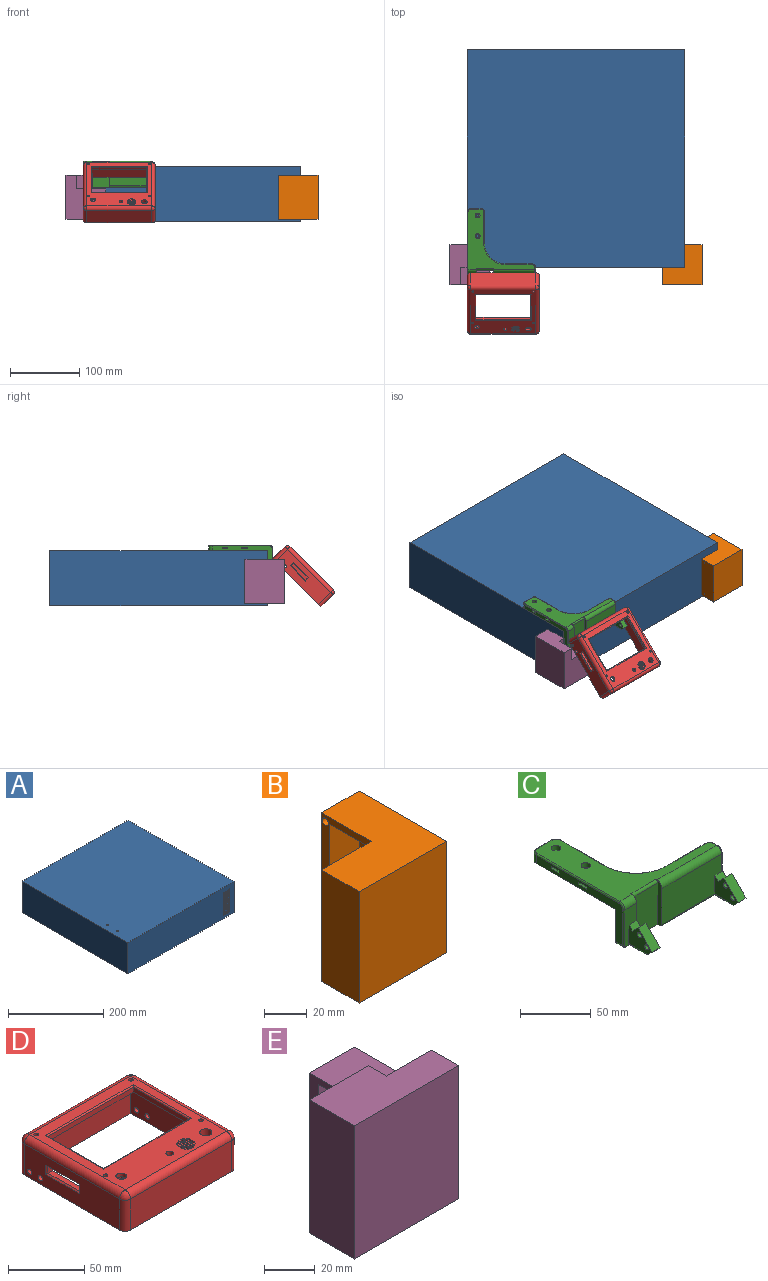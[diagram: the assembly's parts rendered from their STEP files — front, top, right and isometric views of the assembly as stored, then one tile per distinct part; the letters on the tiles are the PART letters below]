
ASSEMBLY  parts=5 mates=11
PART A: 40 faces, bbox 315x315x80 mm
  f0: plane 315x80mm, normal (1,0,0), area 24527.4mm2, adj f1,f3,f4,f5,f21,f22,f23,f24
  f1: plane 315x80mm, normal (0,-1,0), area 24527.4mm2, adj f0,f2,f4,f5,f6,f7,f8,f9
  f2: plane 315x80mm, normal (-1,0,0), area 25200mm2, adj f1,f3,f4,f5
  f3: plane 315x80mm, normal (0,1,0), area 25200mm2, adj f0,f2,f4,f5
  f4: plane 315x315mm, normal (0,0,1), area 99199.9mm2, adj f0,f1,f2,f3,f36,f38
  f5: plane 315x315mm, normal (0,0,-1), area 99225mm2, adj f0,f1,f2,f3
  f6: plane 59x1.5mm, normal (1,0,0), area 88.5mm2, adj f1,f7,f9,f10
  f7: plane 3.8x1.5mm, normal (0,0,1), area 5.7mm2, adj f1,f6,f8,f10
  f8: plane 59x1.5mm, normal (-1,0,0), area 88.5mm2, adj f1,f7,f9,f10
  f9: plane 3.8x1.5mm, normal (0,0,-1), area 5.7mm2, adj f1,f6,f8,f10
  f10: plane 59x3.8mm, normal (0,-1,0), area 224.2mm2, adj f6,f7,f8,f9
  f11: plane 59x1.5mm, normal (1,0,0), area 88.5mm2, adj f1,f12,f14,f15
  f12: plane 3.8x1.5mm, normal (0,0,1), area 5.7mm2, adj f1,f11,f13,f15
  f13: plane 59x1.5mm, normal (-1,0,0), area 88.5mm2, adj f1,f12,f14,f15
  f14: plane 3.8x1.5mm, normal (0,0,-1), area 5.7mm2, adj f1,f11,f13,f15
  f15: plane 59x3.8mm, normal (0,-1,0), area 224.2mm2, adj f11,f12,f13,f14
  f16: plane 3.8x1.5mm, normal (0,0,-1), area 5.7mm2, adj f1,f17,f19,f20
  f17: plane 59x1.5mm, normal (1,0,0), area 88.5mm2, adj f1,f16,f18,f20
  f18: plane 3.8x1.5mm, normal (0,0,1), area 5.7mm2, adj f1,f17,f19,f20
  f19: plane 59x1.5mm, normal (-1,0,0), area 88.5mm2, adj f1,f16,f18,f20
  f20: plane 59x3.8mm, normal (0,-1,0), area 224.2mm2, adj f16,f17,f18,f19
  f21: plane 59x1.5mm, normal (0,1,0), area 88.5mm2, adj f0,f22,f24,f25
  f22: plane 3.8x1.5mm, normal (0,0,1), area 5.7mm2, adj f0,f21,f23,f25
  f23: plane 59x1.5mm, normal (0,-1,0), area 88.5mm2, adj f0,f22,f24,f25
  f24: plane 3.8x1.5mm, normal (0,0,-1), area 5.7mm2, adj f0,f21,f23,f25
  f25: plane 59x3.8mm, normal (1,0,0), area 224.2mm2, adj f21,f22,f23,f24
  f26: plane 59x1.5mm, normal (0,1,0), area 88.5mm2, adj f0,f27,f29,f30
  f27: plane 3.8x1.5mm, normal (0,0,1), area 5.7mm2, adj f0,f26,f28,f30
  f28: plane 59x1.5mm, normal (0,-1,0), area 88.5mm2, adj f0,f27,f29,f30
  f29: plane 3.8x1.5mm, normal (0,0,-1), area 5.7mm2, adj f0,f26,f28,f30
  f30: plane 59x3.8mm, normal (1,0,0), area 224.2mm2, adj f26,f27,f28,f29
  f31: plane 3.8x1.5mm, normal (0,0,-1), area 5.7mm2, adj f0,f32,f34,f35
  f32: plane 59x1.5mm, normal (0,1,0), area 88.5mm2, adj f0,f31,f33,f35
  f33: plane 3.8x1.5mm, normal (0,0,1), area 5.7mm2, adj f0,f32,f34,f35
  f34: plane 59x1.5mm, normal (0,-1,0), area 88.5mm2, adj f0,f31,f33,f35
  f35: plane 59x3.8mm, normal (1,0,0), area 224.2mm2, adj f31,f32,f33,f34
  f36: cylinder r=2mm len=5mm, axis (0,0,1), area 62.8mm2, adj f4,f37
  f37: plane 4x4mm, normal (0,0,1), area 12.6mm2, adj f36
  f38: cylinder r=2mm len=5mm, axis (0,0,1), area 62.8mm2, adj f4,f39
  f39: plane 4x4mm, normal (0,0,1), area 12.6mm2, adj f38
PART B: 21 faces, bbox 57.9x57.9x64 mm
  f0: plane 64x32.9mm, normal (0,1,0), area 406.5mm2, adj f1,f5,f9,f10,f11,f12,f13,f15
  f1: plane 64x25mm, normal (-1,0,0), area 1600mm2, adj f0,f2,f10,f12
  f2: plane 64x57.9mm, normal (0,-1,0), area 3705.6mm2, adj f1,f3,f10,f12
  f3: plane 64x57.9mm, normal (1,0,0), area 3705.6mm2, adj f2,f4,f10,f12
  f4: plane 64x25mm, normal (0,1,0), area 1600mm2, adj f3,f5,f10,f12
  f5: plane 64x32.9mm, normal (-1,0,0), area 406.5mm2, adj f0,f4,f6,f10,f11,f12,f17,f19
  f6: plane 60x20mm, normal (0,-1,0), area 1200mm2, adj f5,f7,f10,f11
  f7: plane 60x47.9mm, normal (-1,0,0), area 2874mm2, adj f6,f8,f10,f11
  f8: plane 60x47.9mm, normal (0,1,0), area 2874mm2, adj f7,f9,f10,f11
  f9: plane 60x20mm, normal (1,0,0), area 1200mm2, adj f0,f8,f10,f11
  f10: plane 57.9x57.9mm, normal (0,0,-1), area 754mm2, adj f0,f1,f2,f3,f4,f5,f6,f7
  f11: plane 47.9x47.9mm, normal (0,0,-1), area 1516mm2, adj f0,f5,f6,f7,f8,f9
  f12: plane 57.9x57.9mm, normal (0,0,1), area 2270mm2, adj f0,f1,f2,f3,f4,f5
  f13: cylinder r=2mm len=5mm, axis (0,1,0), area 62.8mm2, adj f0,f14
  f14: plane 4x4mm, normal (0,1,0), area 12.6mm2, adj f13
  f15: cylinder r=2mm len=5mm, axis (0,1,0), area 62.8mm2, adj f0,f16
  f16: plane 4x4mm, normal (0,1,0), area 12.6mm2, adj f15
  f17: cylinder r=2mm len=5mm, axis (-1,0,0), area 62.8mm2, adj f5,f18
  f18: plane 4x4mm, normal (-1,0,0), area 12.6mm2, adj f17
  f19: cylinder r=2mm len=5mm, axis (-1,0,0), area 62.8mm2, adj f5,f20
  f20: plane 4x4mm, normal (-1,0,0), area 12.6mm2, adj f19
PART C: 71 faces, bbox 99.8x116.7x38.6 mm
  f0: cylinder r=2mm len=4mm, axis (0,0,-1), area 50.3mm2, adj f12,f67
  f1: cylinder r=2mm len=4mm, axis (0,0,-1), area 50.3mm2, adj f12,f69
  f2: cylinder r=5mm len=12mm, axis (-1,0,0), area 94.2mm2, adj f14,f17,f28,f55
  f3: plane 87x35mm, normal (-1,0,0), area 769.6mm2, adj f12,f19,f32,f33,f34,f35,f36,f37
  f4: plane 45x7mm, normal (1,0,0), area 295mm2, adj f12,f18,f32,f33,f34,f36,f37,f38
  f5: plane 60x31mm, normal (0,-1,0), area 1748mm2, adj f6,f29,f30,f43,f46,f66
  f6: plane 8x4.54mm, normal (0,-0.71,0.71), area 40.3mm2, adj f5,f7,f15,f29,f66
  f7: plane 8x5.66mm, normal (0,0.71,0.71), area 64mm2, adj f6,f8,f15,f29
  f8: plane 14.14x14.14mm, normal (0,-0.71,0.71), area 160mm2, adj f7,f9,f15,f29
  f9: plane 8x5.98mm, normal (0,-0.71,-0.71), area 65.2mm2, adj f8,f15,f20,f29,f45,f51
  f10: cylinder r=2mm len=8mm, axis (1,0,0), area 100.5mm2, adj f15,f29
  f11: cylinder r=2mm len=8mm, axis (1,0,0), area 100.5mm2, adj f15,f29
  f12: plane 99x85mm, normal (0,0,-1), area 2646.9mm2, adj f0,f1,f3,f4,f13,f16,f18,f19
  f13: plane 15x7mm, normal (0,1,0), area 105mm2, adj f12,f40,f42,f58
  f14: plane 32x12mm, normal (0,-1,0), area 247.9mm2, adj f2,f21,f27,f28,f48,f52,f53,f54
  f15: plane 35x31.33mm, normal (1,0,0), area 518.1mm2, adj f6,f7,f8,f9,f10,f11,f19,f41
  f16: plane 39x7mm, normal (0,1,0), area 273mm2, adj f12,f18,f41,f62
  f17: plane 97x87mm, normal (0,0,1), area 2613mm2, adj f2,f28,f30,f43,f44,f56,f57,f58
  f18: cylinder r=30mm len=30mm, axis (0,0,1), area 317.8mm2, adj f4,f12,f16,f33,f34,f35,f61
  f19: plane 99x28mm, normal (0,1,0), area 2772mm2, adj f3,f12,f15,f50
  f20: plane 95x23.36mm, normal (0,0,-1), area 485.8mm2, adj f9,f24,f30,f31,f45,f46,f47,f48
  f21: plane 8x3.54mm, normal (0,-0.71,0.71), area 40mm2, adj f14,f22,f27,f28
  f22: plane 8x5.66mm, normal (0,0.71,0.71), area 64mm2, adj f21,f23,f27,f28
  f23: plane 14.14x14.14mm, normal (0,-0.71,0.71), area 160mm2, adj f22,f24,f27,f28
  f24: plane 8x5.98mm, normal (0,-0.71,-0.71), area 65.2mm2, adj f20,f23,f27,f28,f47,f48
  f25: cylinder r=2mm len=8mm, axis (1,0,0), area 100.5mm2, adj f27,f28
  f26: cylinder r=2mm len=8mm, axis (1,0,0), area 100.5mm2, adj f27,f28
  f27: plane 23.33x18.12mm, normal (-1,0,0), area 260.1mm2, adj f14,f21,f22,f23,f24,f25,f26,f48
  f28: plane 36x29.33mm, normal (1,0,0), area 399.5mm2, adj f2,f14,f17,f21,f22,f23,f24,f25
  f29: plane 23.33x18.12mm, normal (-1,0,0), area 260.1mm2, adj f5,f6,f7,f8,f9,f10,f11,f45
  f30: plane 38x6mm, normal (-1,0,0), area 146.6mm2, adj f5,f17,f20,f31,f43,f44,f46
  f31: plane 36x27mm, normal (0,-1,0), area 900.9mm2, adj f20,f28,f30,f44,f47
  f32: plane 25x2mm, normal (0,-1,0), area 50mm2, adj f3,f4,f33,f34
  f33: plane 25.61x8mm, normal (0,0,-1), area 201.2mm2, adj f3,f4,f18,f32,f35
  f34: plane 25.61x8mm, normal (0,0,1), area 201.2mm2, adj f3,f4,f18,f32,f35
  f35: plane 25.61x2mm, normal (0,1,0), area 51.2mm2, adj f3,f18,f33,f34
  f36: plane 25x8mm, normal (0,0,-1), area 200mm2, adj f3,f4,f37,f39
  f37: plane 25x2mm, normal (0,-1,0), area 50mm2, adj f3,f4,f36,f38
  f38: plane 25x8mm, normal (0,0,1), area 200mm2, adj f3,f4,f37,f39
  f39: plane 25x2mm, normal (0,1,0), area 50mm2, adj f3,f4,f36,f38
  f40: cylinder r=5mm len=7mm, axis (0,0,1), area 55mm2, adj f3,f12,f13,f57
  f41: cylinder r=5mm len=7mm, axis (0,0,-1), area 55mm2, adj f12,f15,f16,f63
  f42: cylinder r=5mm len=7mm, axis (0,0,-1), area 55mm2, adj f4,f12,f13,f59
  f43: cylinder r=5mm len=60mm, axis (-1,0,0), area 471.2mm2, adj f5,f17,f30,f65
  f44: cylinder r=2mm len=25mm, axis (-1,0,0), area 78.5mm2, adj f17,f28,f30,f31
  f45: cylinder r=2mm len=21.36mm, axis (0,1,0), area 59.1mm2, adj f9,f20,f29,f46
  f46: cylinder r=2mm len=55mm, axis (1,0,0), area 168.8mm2, adj f5,f20,f30,f45
  f47: cylinder r=2mm len=23.36mm, axis (0,-1,0), area 69.4mm2, adj f20,f24,f28,f31
  f48: cylinder r=2mm len=20.36mm, axis (0,-1,0), area 57.6mm2, adj f14,f20,f24,f27,f52
  f49: cylinder r=2mm len=7mm, axis (0,1,0), area 19.7mm2, adj f3,f20,f50,f53
  f50: cylinder r=2mm len=99mm, axis (-1,0,0), area 306.5mm2, adj f19,f20,f49,f51
  f51: cylinder r=2mm len=27.36mm, axis (0,-1,0), area 79.7mm2, adj f9,f15,f20,f50
  f52: cylinder r=1mm len=5mm, axis (-1,0,0), area 6.3mm2, adj f14,f20,f48,f53
  f53: torus R=1mm, axis (0,-1,0), area 4mm2, adj f14,f49,f52,f54
  f54: cylinder r=1mm len=31mm, axis (0,0,1), area 48.7mm2, adj f3,f14,f53,f55
  f55: torus R=4mm, axis (1,0,0), area 11.4mm2, adj f2,f3,f54,f56
  f56: cylinder r=1mm len=83mm, axis (0,1,0), area 130.4mm2, adj f3,f17,f55,f57
  f57: torus R=4mm, axis (0,0,1), area 11.4mm2, adj f17,f40,f56,f58
  f58: cylinder r=1mm len=15mm, axis (1,0,0), area 23.6mm2, adj f13,f17,f57,f59
  f59: torus R=4mm, axis (0,0,1), area 11.4mm2, adj f17,f42,f58,f60
  f60: cylinder r=1mm len=45mm, axis (0,-1,0), area 70.7mm2, adj f4,f17,f59,f61
  f61: torus R=31mm, axis (0,0,1), area 74.9mm2, adj f17,f18,f60,f62
  f62: cylinder r=1mm len=39mm, axis (1,0,0), area 61.3mm2, adj f16,f17,f61,f63
  f63: torus R=4mm, axis (0,0,1), area 11.4mm2, adj f17,f41,f62,f64
  f64: cylinder r=1mm len=3mm, axis (0,-1,0), area 4.7mm2, adj f15,f17,f63,f65
  f65: torus R=4mm, axis (1,0,0), area 11.4mm2, adj f15,f43,f64,f66
  f66: cylinder r=1mm len=15mm, axis (0,0,-1), area 23mm2, adj f5,f6,f15,f65
  f67: plane 7x7mm, normal (0,0,1), area 25.9mm2, adj f0,f68
  f68: cylinder r=3.5mm len=7mm, axis (0,0,1), area 88mm2, adj f17,f67
  f69: plane 7x7mm, normal (0,0,1), area 25.9mm2, adj f1,f70
  f70: cylinder r=3.5mm len=7mm, axis (0,0,1), area 88mm2, adj f17,f69
PART D: 79 faces, bbox 104x98.5x30 mm
  f0: plane 11.96x3mm, normal (1,0,0), area 35.9mm2, adj f17,f25,f41
  f1: plane 10.91x3mm, normal (1,0,0), area 32.7mm2, adj f17,f25,f39
  f2: plane 7.94x3mm, normal (1,0,0), area 23.8mm2, adj f17,f25,f38
  f3: plane 11.96x3mm, normal (-1,0,0), area 35.9mm2, adj f17,f25,f41
  f4: plane 4.8x3mm, normal (1,0,0), area 14.4mm2, adj f17,f25,f40
  f5: plane 9.75x3mm, normal (1,0,0), area 29.2mm2, adj f17,f25,f35
  f6: plane 11.62x3mm, normal (-1,0,0), area 34.9mm2, adj f17,f25,f39
  f7: plane 9.75x3mm, normal (-1,0,0), area 29.2mm2, adj f17,f25,f38
  f8: plane 4.8x3mm, normal (-1,0,0), area 14.4mm2, adj f17,f25,f36
  f9: plane 11.62x3mm, normal (1,0,0), area 34.9mm2, adj f17,f25,f34
  f10: plane 7.94x3mm, normal (-1,0,0), area 23.8mm2, adj f17,f25,f35
  f11: plane 10.91x3mm, normal (-1,0,0), area 32.7mm2, adj f17,f25,f34
  f12: cylinder r=3.5mm len=7mm, axis (0,0,-1), area 66mm2, adj f25,f30,f31,f32,f33
  f13: plane 94x88.5mm, normal (0,0,-1), area 3924.8mm2, adj f14,f15,f16,f17,f18,f19,f20,f21
  f14: plane 79.5x4mm, normal (0,1,0), area 318mm2, adj f13,f15,f24,f63
  f15: plane 52x4mm, normal (1,0,0), area 208mm2, adj f13,f14,f16,f64
  f16: plane 79.5x4mm, normal (0,-1,0), area 318mm2, adj f13,f15,f24,f66
  f17: cylinder r=6mm len=12mm, axis (0,0,-1), area 114.1mm2, adj f0,f1,f2,f3,f4,f5,f6,f7
  f18: cylinder r=4mm len=8mm, axis (0,0,-1), area 125.7mm2, adj f13,f25
  f19: cylinder r=2.5mm len=5mm, axis (0,0,-1), area 78.5mm2, adj f13,f25
  f20: cylinder r=1.5mm len=5mm, axis (0,0,-1), area 47.1mm2, adj f13,f25
  f21: cylinder r=1.5mm len=5mm, axis (0,0,-1), area 47.1mm2, adj f13,f25
  f22: cylinder r=1.5mm len=5mm, axis (0,0,-1), area 47.1mm2, adj f13,f25
  f23: cylinder r=1.5mm len=5mm, axis (0,0,-1), area 47.1mm2, adj f13,f25
  f24: plane 52x4mm, normal (-1,0,0), area 208mm2, adj f13,f14,f16,f65
  f25: plane 94x88.5mm, normal (0,0,1), area 3723.9mm2, adj f0,f1,f2,f3,f4,f5,f6,f7
  f26: plane 7x2mm, normal (0,1,0), area 14mm2, adj f13,f27,f29,f32,f33
  f27: plane 7x2mm, normal (1,0,0), area 14mm2, adj f13,f26,f28,f30,f33
  f28: plane 7x2mm, normal (0,-1,0), area 14mm2, adj f13,f27,f29,f30,f31
  f29: plane 7x2mm, normal (-1,0,0), area 14mm2, adj f13,f26,f28,f31,f32
  f30: plane 3.5x3.5mm, normal (0,0,-1), area 2.6mm2, adj f12,f27,f28
  f31: plane 3.5x3.5mm, normal (0,0,-1), area 2.6mm2, adj f12,f28,f29
  f32: plane 3.5x3.5mm, normal (0,0,-1), area 2.6mm2, adj f12,f26,f29
  f33: plane 3.5x3.5mm, normal (0,0,-1), area 2.6mm2, adj f12,f26,f27
  f34: plane 11.62x1mm, normal (0,0,-1), area 11.3mm2, adj f9,f11,f17
  f35: plane 9.75x1mm, normal (0,0,-1), area 8.9mm2, adj f5,f10,f17
  f36: plane 4.8x0.5mm, normal (0,0,-1), area 1.6mm2, adj f8,f37
  f37: extruded ~4.8x2mm, area 9.9mm2, adj f13,f17,f36
  f38: plane 9.75x1mm, normal (0,0,-1), area 8.9mm2, adj f2,f7,f17
  f39: plane 11.62x1mm, normal (0,0,-1), area 11.3mm2, adj f1,f6,f17
  f40: plane 4.8x0.5mm, normal (0,0,-1), area 1.6mm2, adj f4,f17
  f41: plane 12x1mm, normal (0,0,-1), area 12mm2, adj f0,f3,f17
  f42: plane 94x25mm, normal (0,-1,0), area 2350mm2, adj f13,f43,f45,f50
  f43: plane 88.5x25mm, normal (1,0,0), area 2027.9mm2, adj f13,f42,f44,f50,f67,f68,f69,f70
  f44: plane 94x25mm, normal (0,1,0), area 2350mm2, adj f13,f43,f45,f50
  f45: plane 88.5x25mm, normal (-1,0,0), area 2187.4mm2, adj f13,f42,f44,f50,f75,f76
  f46: plane 94x25mm, normal (0,1,0), area 2350mm2, adj f50,f51,f54,f62
  f47: plane 88.5x25mm, normal (-1,0,0), area 1954.9mm2, adj f50,f51,f52,f58,f71,f72,f73,f74
  f48: plane 94x25mm, normal (0,-1,0), area 2350mm2, adj f50,f52,f53,f55
  f49: plane 88.5x25mm, normal (1,0,0), area 2187.4mm2, adj f50,f53,f54,f59,f75,f76
  f50: plane 104x98.5mm, normal (0,0,-1), area 1903.5mm2, adj f42,f43,f44,f45,f46,f47,f48,f49
  f51: cylinder r=5mm len=25mm, axis (0,0,-1), area 196.3mm2, adj f46,f47,f50,f60
  f52: cylinder r=5mm len=25mm, axis (0,0,1), area 196.3mm2, adj f47,f48,f50,f56
  f53: cylinder r=5mm len=25mm, axis (0,0,-1), area 196.3mm2, adj f48,f49,f50,f57
  f54: cylinder r=5mm len=25mm, axis (0,0,1), area 196.3mm2, adj f46,f49,f50,f61
  f55: cylinder r=5mm len=94mm, axis (1,0,0), area 738.3mm2, adj f25,f48,f56,f57
  f56: sphere r=5mm, area 39.3mm2, adj f52,f55,f58
  f57: sphere r=5mm, area 39.3mm2, adj f53,f55,f59
  f58: cylinder r=5mm len=88.5mm, axis (0,-1,0), area 695.1mm2, adj f25,f47,f56,f60
  f59: cylinder r=5mm len=88.5mm, axis (0,1,0), area 695.1mm2, adj f25,f49,f57,f61
  f60: sphere r=5mm, area 39.3mm2, adj f51,f58,f62
  f61: sphere r=5mm, area 39.3mm2, adj f54,f59,f62
  f62: cylinder r=5mm len=94mm, axis (-1,0,0), area 738.3mm2, adj f25,f46,f60,f61
  f63: cylinder r=1mm len=81.5mm, axis (1,0,0), area 126mm2, adj f14,f25,f64,f65
  f64: cylinder r=1mm len=54mm, axis (0,-1,0), area 82.8mm2, adj f15,f25,f63,f66
  f65: cylinder r=1mm len=54mm, axis (0,1,0), area 82.8mm2, adj f24,f25,f63,f66
  f66: cylinder r=1mm len=81.5mm, axis (-1,0,0), area 126mm2, adj f16,f25,f64,f65
  f67: plane 5.5x4mm, normal (0,-1,0), area 22mm2, adj f43,f68,f69,f71
  f68: plane 29x4mm, normal (0,0,-1), area 116mm2, adj f43,f67,f70,f72
  f69: plane 29x4mm, normal (0,0,1), area 116mm2, adj f43,f67,f70,f73
  f70: plane 5.5x4mm, normal (0,1,0), area 22mm2, adj f43,f68,f69,f74
  f71: plane 7.5x1mm, normal (-0.71,-0.71,0), area 9.2mm2, adj f47,f67,f72,f73
  f72: plane 31x1mm, normal (-0.71,0,-0.71), area 42.4mm2, adj f47,f68,f71,f74
  f73: plane 31x1mm, normal (-0.71,0,0.71), area 42.4mm2, adj f47,f69,f71,f74
  f74: plane 7.5x1mm, normal (-0.71,0.71,0), area 9.2mm2, adj f47,f70,f72,f73
  f75: cylinder r=2mm len=5mm, axis (1,0,0), area 62.8mm2, adj f45,f49
  f76: cylinder r=2mm len=5mm, axis (1,0,0), area 62.8mm2, adj f45,f49
  f77: cylinder r=2mm len=5mm, axis (1,0,0), area 62.8mm2, adj f43,f47
  f78: cylinder r=2mm len=5mm, axis (1,0,0), area 62.8mm2, adj f43,f47
PART E: 25 faces, bbox 57.9x57.9x64 mm
  f0: plane 41x20mm, normal (0,-1,0), area 820mm2, adj f4,f9,f12,f22
  f1: plane 64x32.9mm, normal (0,1,0), area 463.5mm2, adj f2,f3,f5,f9,f11,f12,f13,f14
  f2: plane 20x10mm, normal (1,0,0), area 200mm2, adj f1,f13,f20,f21
  f3: plane 47.9x20mm, normal (0,0,-1), area 659mm2, adj f1,f4,f10,f11,f23,f24
  f4: plane 60x47.9mm, normal (-1,0,0), area 2096.9mm2, adj f0,f3,f10,f12,f22,f23
  f5: plane 64x25mm, normal (-1,0,0), area 1600mm2, adj f1,f6,f12,f13
  f6: plane 64x57.9mm, normal (0,-1,0), area 3705.6mm2, adj f5,f7,f12,f13
  f7: plane 64x57.9mm, normal (1,0,0), area 2847.6mm2, adj f6,f8,f12,f13,f20,f21
  f8: plane 44x25mm, normal (0,1,0), area 1100mm2, adj f7,f9,f12,f20
  f9: plane 44x32.9mm, normal (-1,0,0), area 291.1mm2, adj f0,f1,f8,f12,f18,f20,f22
  f10: plane 60x47.9mm, normal (0,1,0), area 2874mm2, adj f3,f4,f11,f12
  f11: plane 60x20mm, normal (1,0,0), area 1200mm2, adj f1,f3,f10,f12
  f12: plane 57.9x57.9mm, normal (0,0,-1), area 754mm2, adj f0,f1,f4,f5,f6,f7,f8,f9
  f13: plane 57.9x25mm, normal (0,0,1), area 1197.5mm2, adj f1,f2,f5,f6,f7,f21
  f14: cylinder r=2mm len=5mm, axis (0,1,0), area 62.8mm2, adj f1,f15
  f15: plane 4x4mm, normal (0,1,0), area 12.6mm2, adj f14
  f16: cylinder r=2mm len=5mm, axis (0,1,0), area 62.8mm2, adj f1,f17
  f17: plane 4x4mm, normal (0,1,0), area 12.6mm2, adj f16
  f18: cylinder r=2mm len=5mm, axis (-1,0,0), area 62.8mm2, adj f9,f19
  f19: plane 4x4mm, normal (-1,0,0), area 12.6mm2, adj f18
  f20: plane 42.9x25mm, normal (0,0,1), area 1072.5mm2, adj f2,f7,f8,f9,f21
  f21: plane 25x20mm, normal (0,1,0), area 500mm2, adj f2,f7,f13,f20
  f22: plane 40.9x23mm, normal (0,0,-1), area 857mm2, adj f0,f1,f4,f9,f23,f24
  f23: plane 23x19mm, normal (0,-1,0), area 437mm2, adj f3,f4,f22,f24
  f24: plane 19x13mm, normal (-1,0,0), area 247mm2, adj f1,f3,f22,f23
PLACE A rot(axis=(0,0,-1),0deg) t=(158.19,-348.98,17.47)mm
PLACE B rot(axis=(0,0,1),0deg) t=(440.29,-373.98,21)mm
PLACE C t=(153.19,-353.98,97.47)mm
PLACE D rot(axis=(1,0,0),45deg) t=(163.19,-437.84,29.96)mm
PLACE E rot(axis=(0,0,-1),90deg) t=(133.19,-296.58,21)mm
MATE cylindrical D.f75 <-> C.f11  axis (-1,0,0) through (168.19,-364.65,74.87)mm
MATE cylindrical C.f0 <-> A.f38  axis (0,0,1) through (183.19,-263.98,105.47)mm
MATE planar A.f2 <-> E.f1  axis (-1,0,0) through (168.19,-181.48,57.47)mm
MATE planar A.f1 <-> B.f0  axis (0,-1,0) through (321.98,-338.98,57.54)mm
MATE cylindrical D.f76 <-> C.f10  axis (-1,0,0) through (168.19,-357.58,81.94)mm
MATE cylindrical A.f36 <-> C.f1  axis (0,0,1) through (183.19,-293.98,92.47)mm
MATE planar B.f12 <-> E.f13  axis (0,0,1) through (485.2,-340.99,85)mm
MATE parallel E.f13 <-> B.f12  axis (0,0,1) through (154.12,-332.09,85)mm
MATE planar A.f0 <-> B.f5  axis (1,0,0) through (483.19,-177.77,57.54)mm
MATE planar C.f12 <-> A.f4  axis (0,0,-1) through (193.19,-303.98,97.47)mm
MATE planar C.f27 <-> D.f43  axis (-1,0,0) through (173.19,-356.31,76.3)mm
